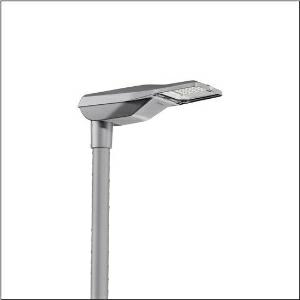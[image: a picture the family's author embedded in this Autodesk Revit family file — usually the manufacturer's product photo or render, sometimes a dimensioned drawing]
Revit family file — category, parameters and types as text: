
# Revit family: streetlight_sl_21_iq_micro___p0_8ab_5xe1r31d08cb_f933
name_source: partatom
category: Lighting Fixtures
units: mm (PartAtom-declared; Revit-internal decimal feet)

## family parameters
Cut with Voids When Loaded = No
Host = Face
Light Source = No
Part Type = Normal
Room Calculation Point = No
Round Connector Dimension = Use Diameter
Shared = No

## types (1)
- --- (1 x LED, 2510 lm, 19.4 W, 3000K)
    Apparent Load = 19 VA
    CIE Flux Codes = 36 71 98 100 100
    Color Rendering = 70
    Color Temperature = 3000K
    Default Elevation = 1800 mm
    Description = Streetlight SL 21 iQ micro, mast luminaire, primary light control with lens, of PMMA, primary optical cover: cover, of toughened safety glass, transparent, light distribution: P0.8aB, light emission: direct distribution, primary light characteristic: asymmetric, installation type: post-top, side-entry, LED, High Power LED, rated luminous flux: 2.510lm, luminous efficacy: 129lm/W, light colour: 730, colour temperature: 3000K, control gear: iQ-Comfort, control: pre-setting: linear dimming characteristic, Auto-Match, Temp-Guard, Lumen-Switch, Night-Set, Smart-Wire, Light-Fading, Desk-Remote (wireless, voltage-free reading and setting of iQ features in the workshop via application-optimized NFC function/RFID function), optimised constant luminous flux control (CLO 2.0), mains connection: 220..240V, AC, 50/60Hz, start of lifetime: 19W, end of service life: 20W, reduction: 10W, luminaire housing, of diecast aluminium, powder-coated, SITECO metallic grey (DB 702S), corrosivity category C5 high according to DIN EN ISO 12944, please order mast flange separately, inclination adjustable: 0°, 5°, 10°, 15°, sealing non-destructively replaceable, multi-level sealing system, length: 528mm, width: 235mm, height: 110mm, mast flange for spigot size: 42mm (side-entry): 5XC10008XM4, 60/48mm (side-entry/post-top): 5XC10108XM2, 76/60mm (side-entry/post-top): 5XC10108XM1, protection rating (complete): IP66, insulation class (complete): insulation class II (safety insulation), certification: CE, ENEC, ENEC+, VDE, impact resistance: IK10, permissible operating ambient temperature for outdoor applications: -40..+50°C, standard-compliant lighting for roads and squares, packaging unit: 1 piece

Light Distribution: P0.8aB
    Height = 110 mm
    Lamp = 1 x LED
    Lamp Light Flux = 2510 lm
    Lamp Power = 19.4 W
    Lamp count = 1
    Length = 528 mm
    Luminous efficacy = 129 lm/W
    Manufacturer = Siteco
    ModVariant = No
    Model = 5XE1R31D08CB
    Number of Poles = 1
    OnlyDefault = Yes
    Power Factor = 1
    Product Name = Streetlight SL 21 iQ micro | P0.8aB
    Product group = mast luminaire | pylon top
    ProductGroupID = 6100
    Protection Class = Protection class II
    Protection Degree = IP 66
    RLX_Detail_Level = 1
    RLX_Emergency_Light_Flux = 0 lm
    RLX_Emergency_Type = 0
    RLX_Emergency_Type_DB = No
    RlxData = <blob elided: 98285 chars, md5=ab55b244>
    Socket = socket
    Standby Power = 0 W
    System Light Flux = 2510 lm
    System Power = 19 W
    Type Comments = factory setting: luminous flux: 100 % | dim-lin: 254 | 387 mA
    Type Image = l_1006881.jpg
    URL = http://relux.com
    VarID = @adj_082489
    Voltage = 0 V
    Weight = 0.00 kg
    Width = 235 mm

## geometry (parser evidence)
native form markers: Blend x4, Sweep x10
no freeform markers — native parametric forms only
